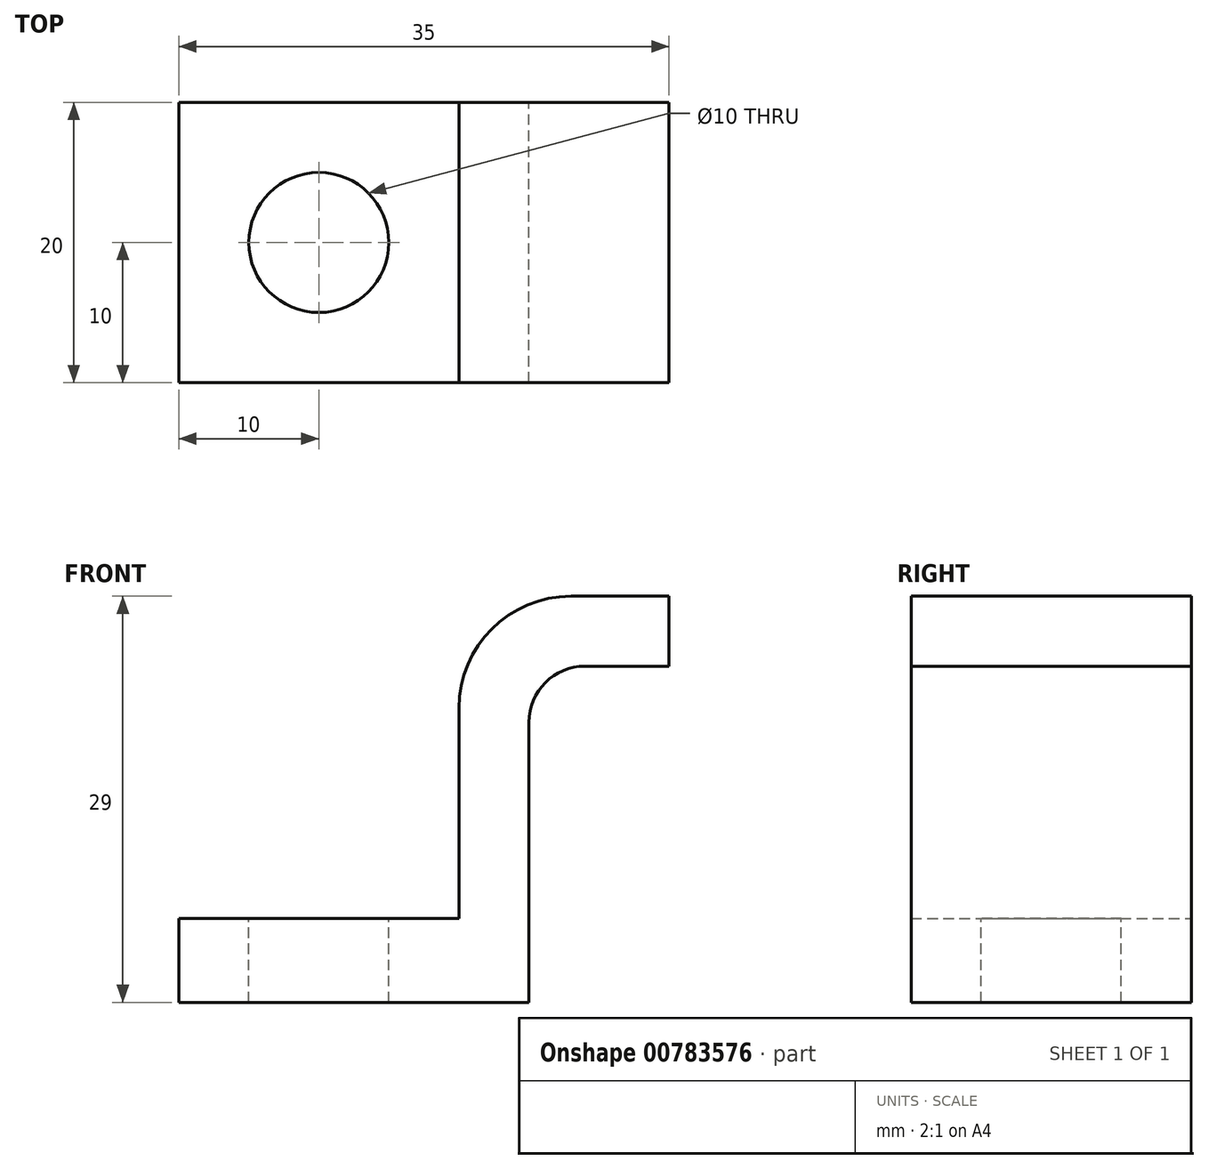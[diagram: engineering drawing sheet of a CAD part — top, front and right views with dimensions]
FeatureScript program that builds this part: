
annotation { "Feature Type Name" : "Feature", "Feature Type Description" : "" }
export const myFeature = defineFeature(function(context is Context, id is Id, definition is map)
    precondition{}
    {
        {
            var Q0;
            Q0=qCreatedBy(makeId("Front.planeOp"),FACE);
            var sketch = newSketch(context, id + "F0", { "sketchPlane" : qUnion([Q0])});
            skLineSegment(sketch, "E0", {"start": v(-10, 0) * mm, "end": v(-10, -6) * mm});
            skLineSegment(sketch, "E1", {"start": v(-10, -6) * mm, "end": v(15, -6) * mm});
            skLineSegment(sketch, "E2", {"start": v(15, -6) * mm, "end": v(15, 14) * mm});
            skLineSegment(sketch, "E3", {"start": v(19, 18) * mm, "end": v(25, 18) * mm});
            skLineSegment(sketch, "E4", {"start": v(25, 18) * mm, "end": v(25, 23) * mm});
            skLineSegment(sketch, "E5", {"start": v(25, 23) * mm, "end": v(18, 23) * mm});
            skLineSegment(sketch, "E6", {"start": v(10, 15) * mm, "end": v(10, 0) * mm});
            skLineSegment(sketch, "E7", {"start": v(10, 0) * mm, "end": v(-10, 0) * mm});
            skPoint(sketch, "E8.visualSharp", {"position": v(10, 23) * mm});
            skArc(sketch, "E8.filletArc", {"start": v(18, 23) * mm, "mid": v(12.34, 20.66) * mm, "end": v(10, 15) * mm});
            skLineSegment(sketch, "E9", {"start": v(0, 0) * mm, "end": v(0, 12.47) * mm, "construction": true});
            skPoint(sketch, "E10.visualSharp", {"position": v(15, 18) * mm});
            skArc(sketch, "E10.filletArc", {"start": v(19, 18) * mm, "mid": v(16.17, 16.83) * mm, "end": v(15, 14) * mm});
            skSolve(sketch);
        }
        {
            var Q0;
            Q0 = qSketchRegion(id + "F0", true);
            extrude(context, id + "F1", {"entities" : qUnion([Q0]), "endBound" : BoundingType.SYMMETRIC, "depth" : 20 * mm, "offsetDistance" : 25 * mm});
        }
        {
            var Q0;
            Q0=makeQuery(id+"F1.opExtrude","SWEPT_FACE",FACE,{"disambiguationData":[OSD([sQuery(id+"F0.wireOp",EDGE,"E7")])]});
            var sketch = newSketch(context, id + "F2", { "sketchPlane" : qUnion([Q0])});
            skPoint(sketch, "E11", {"position": v(0, 0) * mm});
            skSolve(sketch);
        }
        {
            var Q0;
            Q0=sQuery(id+"F2.wireOp",VERTEX,"E11");
            var Q1;
            Q1=makeQuery(id+"F1.opExtrude","SWEPT_BODY",BODY,{"disambiguationData":[OSD([sQuery(id+"F0.wireOp",EDGE,"E0"),sQuery(id+"F0.wireOp",EDGE,"E1"),sQuery(id+"F0.wireOp",EDGE,"E2"),sQuery(id+"F0.wireOp",EDGE,"E3"),sQuery(id+"F0.wireOp",EDGE,"E4"),sQuery(id+"F0.wireOp",EDGE,"E5"),sQuery(id+"F0.wireOp",EDGE,"E6"),sQuery(id+"F0.wireOp",EDGE,"E7"),sQuery(id+"F0.wireOp",EDGE,"E8.filletArc"),sQuery(id+"F0.wireOp",EDGE,"E10.filletArc")])]});
            hole(context, id + "F3", {"style" : HoleStyle.SIMPLE, "endStyle" : HoleEndStyle.BLIND, "holeDiameter" : 10 * mm, "majorDiameter" : 5 * mm, "holeDepth" : 12 * mm, "isTappedThrough" : true, "tappedDepth" : 12 * mm, "tapClearance" : 3, "locations" : qUnion([Q0]), "scope" : qUnion([Q1])});
        }
    });
